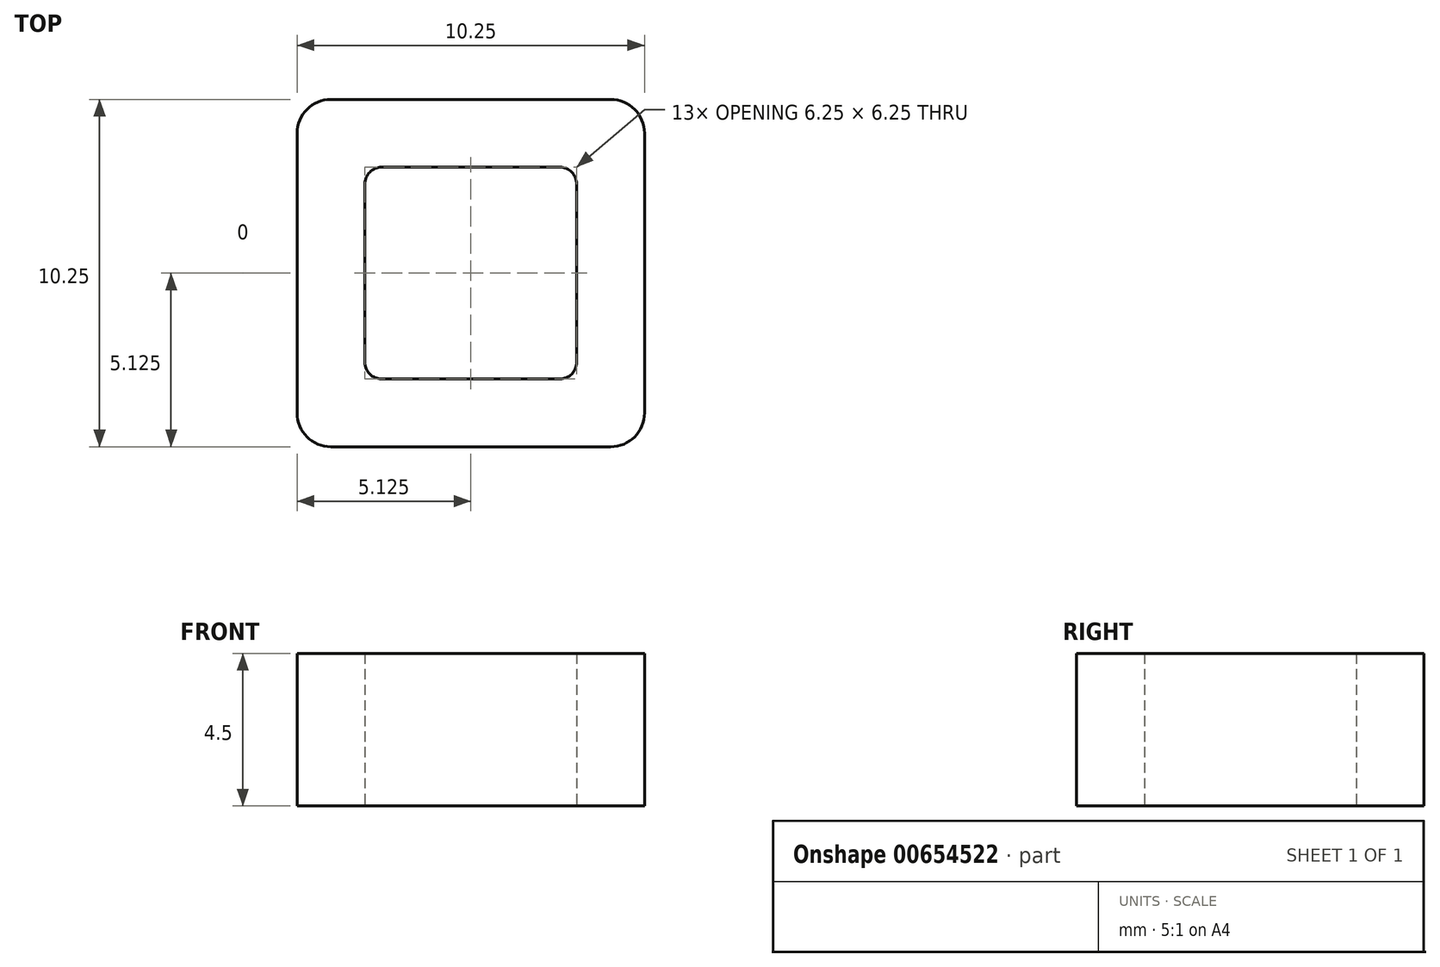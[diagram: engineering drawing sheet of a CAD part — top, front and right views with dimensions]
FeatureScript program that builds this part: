
annotation { "Feature Type Name" : "Feature", "Feature Type Description" : "" }
export const myFeature = defineFeature(function(context is Context, id is Id, definition is map)
    precondition{}
    {
        {
            var Q0;
            Q0=qCreatedBy(makeId("Top.planeOp"),FACE);
            var sketch = newSketch(context, id + "F0", { "sketchPlane" : qUnion([Q0])});
            skLineSegment(sketch, "E0.bottom", {"start": v(0, 0) * mm, "end": v(6.25, 0) * mm});
            skLineSegment(sketch, "E0.top", {"start": v(0, 6.25) * mm, "end": v(6.25, 6.25) * mm});
            skLineSegment(sketch, "E0.left", {"start": v(0, 0) * mm, "end": v(0, 6.25) * mm});
            skLineSegment(sketch, "E0.right", {"start": v(6.25, 0) * mm, "end": v(6.25, 6.25) * mm});
            skLineSegment(sketch, "E1.0", {"start": v(-2, -2) * mm, "end": v(-2, 8.25) * mm});
            skLineSegment(sketch, "E1.1", {"start": v(-2, -2) * mm, "end": v(8.25, -2) * mm});
            skLineSegment(sketch, "E1.2", {"start": v(8.25, -2) * mm, "end": v(8.25, 8.25) * mm});
            skLineSegment(sketch, "E1.3", {"start": v(-2, 8.25) * mm, "end": v(8.25, 8.25) * mm});
            skSolve(sketch);
        }
        {
            var Q0;
            Q0=makeQuery(id+"F0.imprint","IMPRINT",FACE,{"disambiguationData":[TD([[makeQuery(id+"F0.imprint","IMPRINT",EDGE,{"derivedFrom":sQuery(id+"F0.wireOp",EDGE,"E0.bottom")}),-1.0]])]});
            extrude(context, id + "F1", {"entities" : qUnion([Q0]), "depth" : 4.5 * mm, "offsetDistance" : 25 * mm});
        }
        {
            var Q0;
            Q0=makeQuery(id+"F1.opExtrude","SWEPT_EDGE",EDGE,{"disambiguationData":[OSD([sQuery(id+"F0.wireOp",EDGE,"E1.0"),sQuery(id+"F0.wireOp",EDGE,"E1.1")])]});
            var Q1;
            Q1=makeQuery(id+"F1.opExtrude","SWEPT_EDGE",EDGE,{"disambiguationData":[OSD([sQuery(id+"F0.wireOp",EDGE,"E1.1"),sQuery(id+"F0.wireOp",EDGE,"E1.2")])]});
            var Q2;
            Q2=makeQuery(id+"F1.opExtrude","SWEPT_EDGE",EDGE,{"disambiguationData":[OSD([sQuery(id+"F0.wireOp",EDGE,"E1.2"),sQuery(id+"F0.wireOp",EDGE,"E1.3")])]});
            var Q3;
            Q3=makeQuery(id+"F1.opExtrude","SWEPT_EDGE",EDGE,{"disambiguationData":[OSD([sQuery(id+"F0.wireOp",EDGE,"E1.0"),sQuery(id+"F0.wireOp",EDGE,"E1.3")])]});
            fillet(context, id + "F2", {"entities" : qUnion([Q0, Q1, Q2, Q3]), "radius" : 1 * mm, "tangentPropagation" : true, "allowEdgeOverflow" : false});
        }
        {
            var Q0;
            Q0=makeQuery(id+"F1.opExtrude","SWEPT_EDGE",EDGE,{"disambiguationData":[OSD([sQuery(id+"F0.wireOp",EDGE,"E0.top"),sQuery(id+"F0.wireOp",EDGE,"E0.left")])]});
            var Q1;
            Q1=makeQuery(id+"F1.opExtrude","SWEPT_EDGE",EDGE,{"disambiguationData":[OSD([sQuery(id+"F0.wireOp",EDGE,"E0.top"),sQuery(id+"F0.wireOp",EDGE,"E0.right")])]});
            var Q2;
            Q2=makeQuery(id+"F1.opExtrude","SWEPT_EDGE",EDGE,{"disambiguationData":[OSD([sQuery(id+"F0.wireOp",EDGE,"E0.bottom"),sQuery(id+"F0.wireOp",EDGE,"E0.left")])]});
            var Q3;
            Q3=makeQuery(id+"F1.opExtrude","SWEPT_EDGE",EDGE,{"disambiguationData":[OSD([sQuery(id+"F0.wireOp",EDGE,"E0.bottom"),sQuery(id+"F0.wireOp",EDGE,"E0.right")])]});
            fillet(context, id + "F3", {"entities" : qUnion([Q0, Q1, Q2, Q3]), "radius" : 0.5 * mm, "tangentPropagation" : true, "allowEdgeOverflow" : false});
        }
    });
